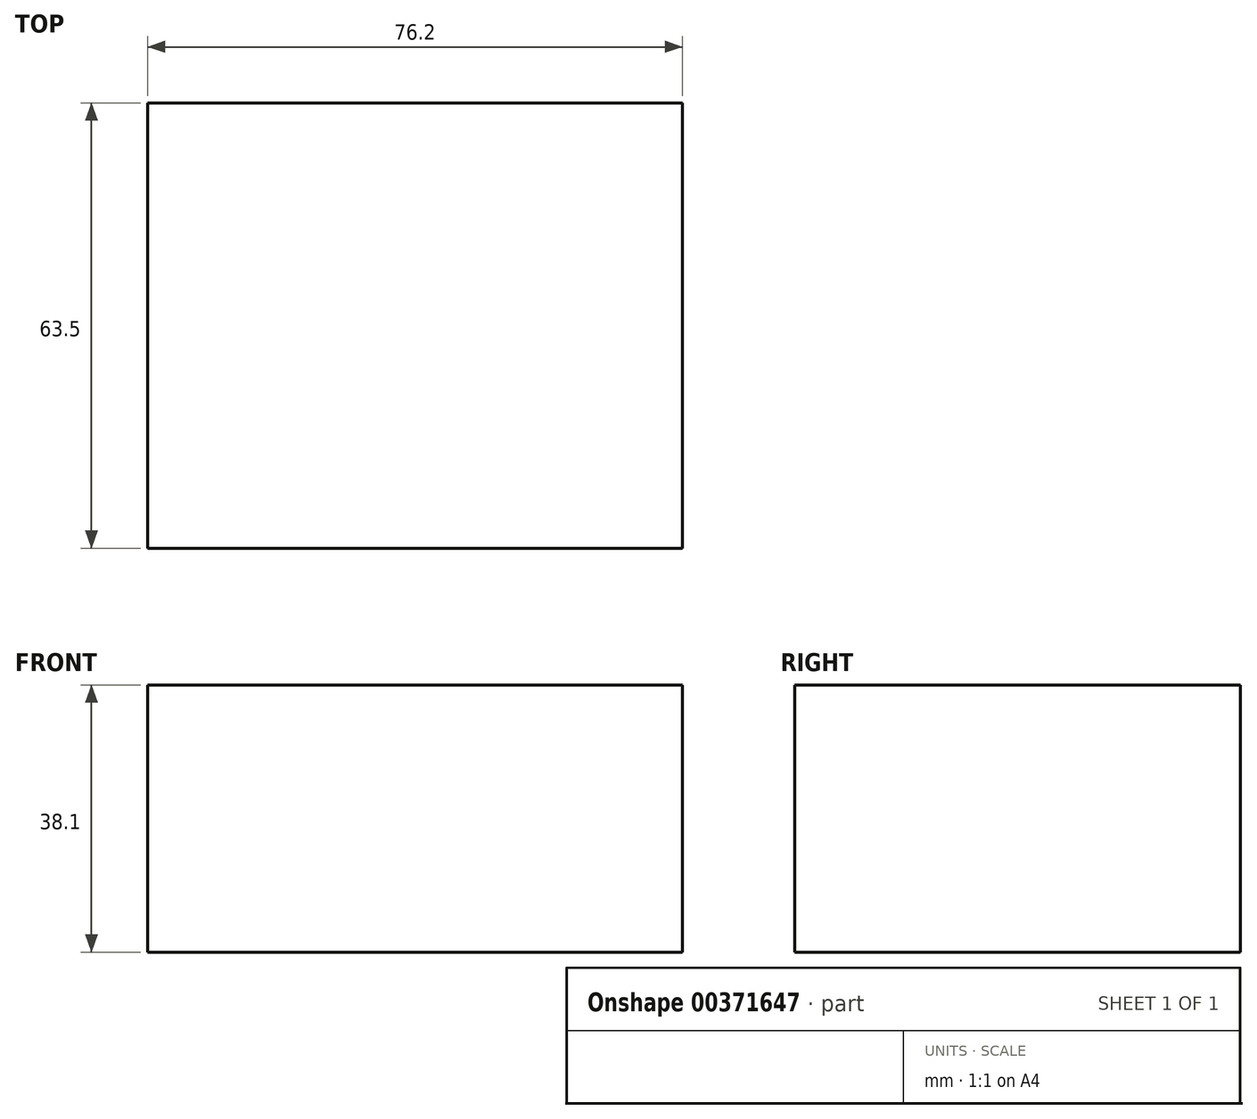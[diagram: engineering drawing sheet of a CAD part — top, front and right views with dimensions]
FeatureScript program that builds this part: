
annotation { "Feature Type Name" : "Feature", "Feature Type Description" : "" }
export const myFeature = defineFeature(function(context is Context, id is Id, definition is map)
    precondition{}
    {
        {
            var Q0;
            Q0=qCreatedBy(makeId("Front.planeOp"),FACE);
            var sketch = newSketch(context, id + "F0", { "sketchPlane" : qUnion([Q0])});
            skLineSegment(sketch, "E0.bottom", {"start": v(31.75, 50.8) * mm, "end": v(107.95, 50.8) * mm});
            skLineSegment(sketch, "E0.top", {"start": v(31.75, 12.7) * mm, "end": v(107.95, 12.7) * mm});
            skLineSegment(sketch, "E0.left", {"start": v(31.75, 50.8) * mm, "end": v(31.75, 12.7) * mm});
            skLineSegment(sketch, "E0.right", {"start": v(107.95, 50.8) * mm, "end": v(107.95, 12.7) * mm});
            skSolve(sketch);
        }
        {
            var Q0;
            Q0 = qSketchRegion(id + "F0", true);
            extrude(context, id + "F1", {"entities" : qUnion([Q0]), "depth" : 63.5 * mm});
        }
    });
